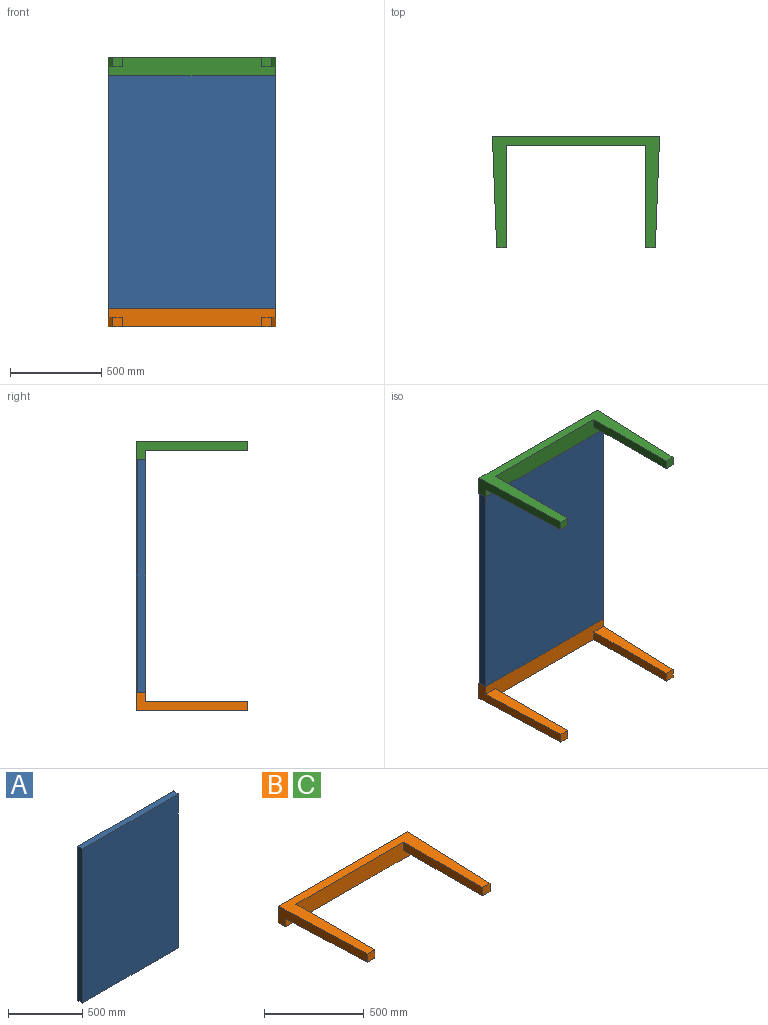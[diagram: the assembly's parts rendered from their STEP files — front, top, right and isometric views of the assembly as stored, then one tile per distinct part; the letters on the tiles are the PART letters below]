
ASSEMBLY  parts=3 mates=1
PART A: 10 faces, bbox 914x50.8x1270 mm
  f0: plane 1270x910.49mm, normal (0,-1,0), area 1156325.2mm2, adj f1,f3,f4,f5
  f1: plane 1270x45.72mm, normal (1,-0.04,0), area 58112.1mm2, adj f0,f4,f5,f7
  f2: plane 1260.22x904.24mm, normal (0,1,0), area 1139544.3mm2, adj f6,f7,f8,f9
  f3: plane 1270x45.72mm, normal (-1,-0.04,0), area 58112.1mm2, adj f0,f4,f5,f8
  f4: plane 914.01x45.91mm, normal (0,0,-1), area 41883.2mm2, adj f0,f1,f3,f7,f8,f9
  f5: plane 914.01x45.91mm, normal (0,0,1), area 41883.2mm2, adj f0,f1,f3,f6,f7,f8
  f6: plane 913.65x4.89mm, normal (0,0.71,0.71), area 6283.7mm2, adj f2,f5,f7,f8
  f7: plane 1270x5.08mm, normal (0.72,0.69,0), area 8913.7mm2, adj f1,f2,f4,f5,f6,f9
  f8: plane 1270x5.08mm, normal (-0.72,0.69,0), area 8913.7mm2, adj f2,f3,f4,f5,f6,f9
  f9: plane 913.65x4.89mm, normal (0,0.71,-0.71), area 6283.7mm2, adj f2,f4,f7,f8
PART B: 12 faces, bbox 914.4x609.6x101.6 mm
  f0: plane 558.8x74.25mm, normal (0,0,-1), area 35483.8mm2, adj f2,f7,f8,f9
  f1: plane 558.8x74.25mm, normal (0,0,-1), area 35483.8mm2, adj f4,f5,f6,f7
  f2: plane 609.6x101.6mm, normal (1,-0.04,0), area 33573.1mm2, adj f0,f3,f7,f9,f10,f11
  f3: plane 914.4x101.6mm, normal (0,1,0), area 92903mm2, adj f2,f4,f10,f11
  f4: plane 609.6x101.6mm, normal (-1,-0.04,0), area 33573.1mm2, adj f1,f3,f5,f7,f10,f11
  f5: plane 52.75x50.8mm, normal (0,-1,0), area 2679.9mm2, adj f1,f4,f6,f10
  f6: plane 558.8x50.8mm, normal (1,0,0), area 28387mm2, adj f1,f5,f7,f10
  f7: plane 910.49x101.6mm, normal (0,-1,0), area 84962.6mm2, adj f0,f1,f2,f4,f6,f8,f10,f11
  f8: plane 558.8x50.8mm, normal (-1,0,0), area 28387mm2, adj f0,f7,f9,f10
  f9: plane 52.75x50.8mm, normal (0,-1,0), area 2679.9mm2, adj f0,f2,f8,f10
  f10: plane 914.4x609.6mm, normal (0,0,1), area 117319.9mm2, adj f2,f3,f4,f5,f6,f7,f8,f9
  f11: plane 914.4x50.8mm, normal (0,0,-1), area 46352.3mm2, adj f2,f3,f4,f7
PART C: same geometry as B
PLACE A t=(-88.89,-746.79,-7.16)mm
PLACE B rot(axis=(0,1,0),180deg) t=(-927.09,-746.7,-1378.76)mm
PLACE C t=(-88.89,-746.79,-7.16)mm
MATE parallel B.f11 <-> A.f4  axis (0,0,1) through (-507.99,-441.88,-1327.96)mm
